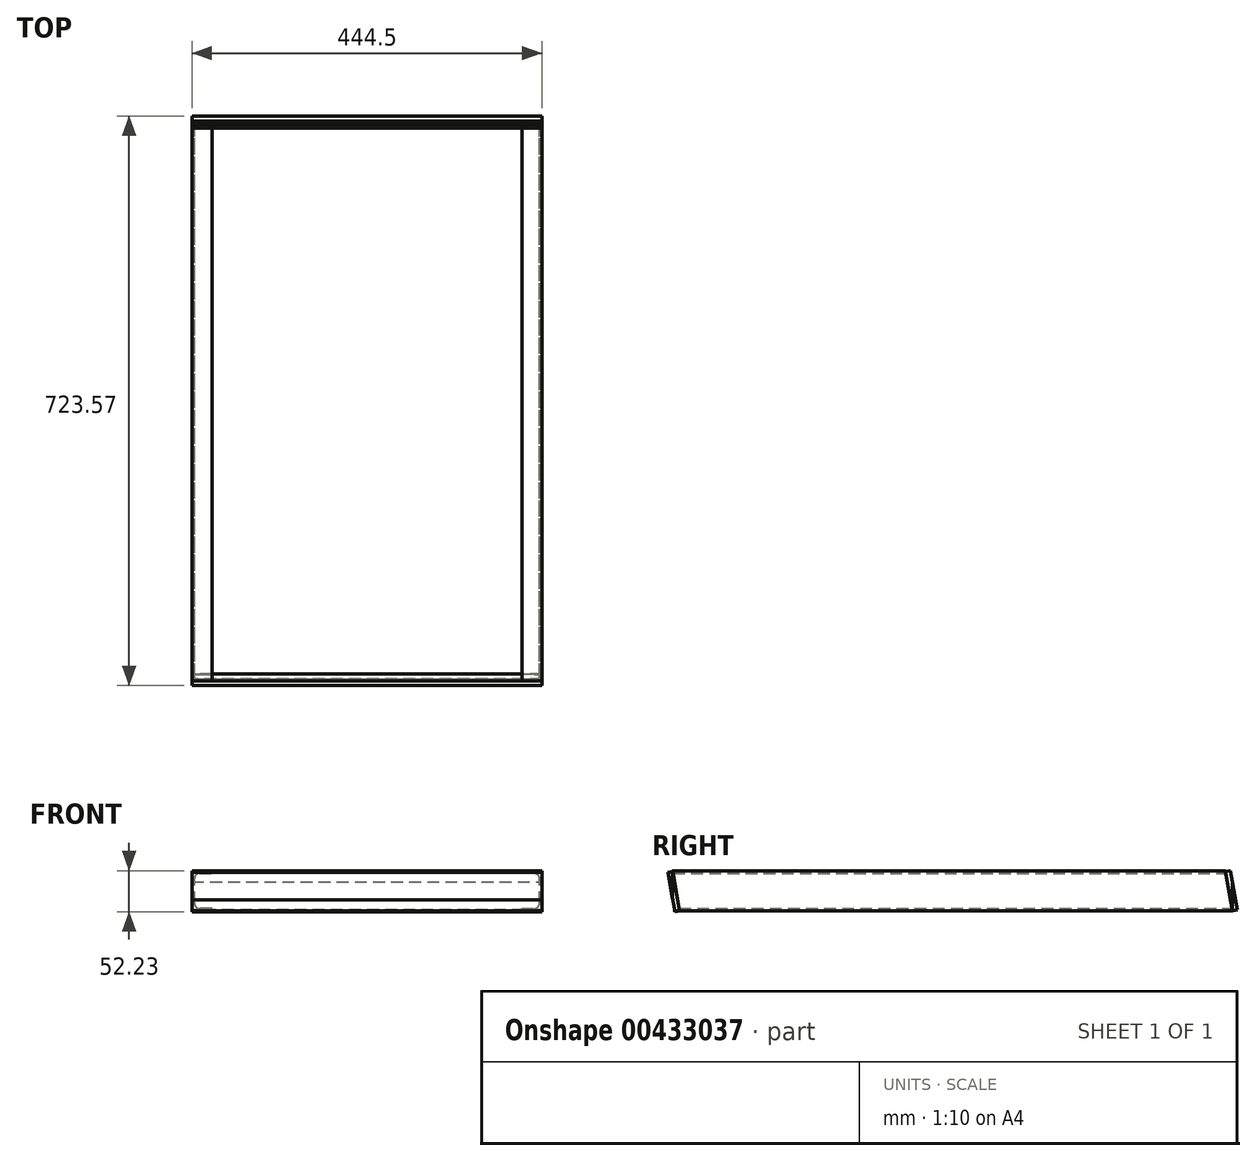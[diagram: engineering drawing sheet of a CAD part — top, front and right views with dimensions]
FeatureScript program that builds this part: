
annotation { "Feature Type Name" : "Feature", "Feature Type Description" : "" }
export const myFeature = defineFeature(function(context is Context, id is Id, definition is map)
    precondition{}
    {
        {
            var Q0;
            Q0=qCreatedBy(makeId("Front.planeOp"),FACE);
            var sketch = newSketch(context, id + "F0", { "sketchPlane" : qUnion([Q0])});
            skLineSegment(sketch, "E0", {"start": v(0, 0) * mm, "end": v(0, 50.8) * mm});
            skLineSegment(sketch, "E1", {"start": v(0, 50.8) * mm, "end": v(25.4, 50.8) * mm});
            skLineSegment(sketch, "E2", {"start": v(25.4, 50.8) * mm, "end": v(25.4, 47.63) * mm});
            skLineSegment(sketch, "E3", {"start": v(25.4, 47.63) * mm, "end": v(9.52, 47.63) * mm});
            skLineSegment(sketch, "E4", {"start": v(3.17, 41.28) * mm, "end": v(3.18, 9.52) * mm});
            skLineSegment(sketch, "E5", {"start": v(9.53, 3.17) * mm, "end": v(25.4, 3.18) * mm});
            skLineSegment(sketch, "E6", {"start": v(25.4, 3.18) * mm, "end": v(25.4, 0) * mm});
            skLineSegment(sketch, "E7", {"start": v(25.4, 0) * mm, "end": v(0, 0) * mm});
            skLineSegment(sketch, "E8", {"start": v(419.1, 0) * mm, "end": v(444.5, 0) * mm});
            skLineSegment(sketch, "E9", {"start": v(444.5, 0) * mm, "end": v(444.5, 50.8) * mm});
            skLineSegment(sketch, "E10", {"start": v(444.5, 50.8) * mm, "end": v(419.1, 50.8) * mm});
            skLineSegment(sketch, "E11", {"start": v(419.1, 50.8) * mm, "end": v(419.1, 47.63) * mm});
            skLineSegment(sketch, "E12", {"start": v(419.1, 47.63) * mm, "end": v(434.98, 47.63) * mm});
            skLineSegment(sketch, "E13", {"start": v(441.33, 41.28) * mm, "end": v(441.33, 9.53) * mm});
            skLineSegment(sketch, "E14", {"start": v(434.98, 3.18) * mm, "end": v(419.1, 3.18) * mm});
            skLineSegment(sketch, "E15", {"start": v(419.1, 3.18) * mm, "end": v(419.1, 0) * mm});
            skPoint(sketch, "E16.visualSharp", {"position": v(3.17, 47.62) * mm});
            skArc(sketch, "E16.filletArc", {"start": v(9.52, 47.63) * mm, "mid": v(5.03, 45.77) * mm, "end": v(3.17, 41.28) * mm});
            skPoint(sketch, "E17.visualSharp", {"position": v(3.18, 3.17) * mm});
            skArc(sketch, "E17.filletArc", {"start": v(3.18, 9.52) * mm, "mid": v(5.03, 5.03) * mm, "end": v(9.53, 3.17) * mm});
            skPoint(sketch, "E18.visualSharp", {"position": v(441.33, 47.63) * mm});
            skArc(sketch, "E18.filletArc", {"start": v(441.33, 41.28) * mm, "mid": v(439.47, 45.77) * mm, "end": v(434.98, 47.63) * mm});
            skPoint(sketch, "E19.visualSharp", {"position": v(441.33, 3.18) * mm});
            skArc(sketch, "E19.filletArc", {"start": v(434.98, 3.18) * mm, "mid": v(439.47, 5.03) * mm, "end": v(441.33, 9.53) * mm});
            skSolve(sketch);
        }
        {
            var Q0;
            Q0=makeQuery(id+"F0.imprint","IMPRINT",FACE,{"disambiguationData":[TD([[makeQuery(id+"F0.imprint","IMPRINT",EDGE,{"derivedFrom":sQuery(id+"F0.wireOp",EDGE,"E0")}),-1.0]])]});
            var Q1;
            Q1=makeQuery(id+"F0.imprint","IMPRINT",FACE,{"disambiguationData":[TD([[makeQuery(id+"F0.imprint","IMPRINT",EDGE,{"derivedFrom":sQuery(id+"F0.wireOp",EDGE,"E8")}),1.0]])]});
            extrude(context, id + "F1", {"entities" : qUnion([Q0, Q1]), "depth" : 711.2 * mm, "offsetDistance" : 25.4 * mm});
        }
        {
            var Q0;
            Q0=qCreatedBy(makeId("Right.planeOp"),FACE);
            var sketch = newSketch(context, id + "F2", { "sketchPlane" : qUnion([Q0])});
            skLineSegment(sketch, "E20", {"start": v(0, 0) * mm, "end": v(0, 50.8) * mm});
            skLineSegment(sketch, "E21", {"start": v(0, 50.8) * mm, "end": v(-8.96, 50.8) * mm});
            skLineSegment(sketch, "E22", {"start": v(-8.96, 50.8) * mm, "end": v(0, 0) * mm});
            skLineSegment(sketch, "E23", {"start": v(-702.24, 0) * mm, "end": v(-711.2, 50.8) * mm});
            skLineSegment(sketch, "E24", {"start": v(-711.2, 50.8) * mm, "end": v(-711.2, 0) * mm});
            skLineSegment(sketch, "E25", {"start": v(-711.2, 0) * mm, "end": v(-702.24, 0) * mm});
            skSolve(sketch);
        }
        {
            var Q0;
            Q0=makeQuery(id+"F2.imprint","IMPRINT",FACE,{"disambiguationData":[TD([[makeQuery(id+"F2.imprint","IMPRINT",EDGE,{"derivedFrom":sQuery(id+"F2.wireOp",EDGE,"E20")}),1.0]])]});
            var Q1;
            Q1=makeQuery(id+"F2.imprint","IMPRINT",FACE,{"disambiguationData":[TD([[makeQuery(id+"F2.imprint","IMPRINT",EDGE,{"derivedFrom":sQuery(id+"F2.wireOp",EDGE,"E23")}),1.0]])]});
            var Q2;
            Q2=makeQuery(id+"F1.opExtrude","SWEPT_FACE",FACE,{"disambiguationData":[OSD([sQuery(id+"F0.wireOp",EDGE,"E9")])]});
            extrude(context, id + "F3", {"entities" : qUnion([Q0, Q1]), "operationType" : NewBodyOperationType.REMOVE, "endBound" : BoundingType.THROUGH_ALL, "endBoundEntityFace" : qUnion([Q2]), "depth" : 25.4 * mm, "offsetDistance" : 25.4 * mm});
        }
        {
            var Q0;
            Q0=qCreatedBy(makeId("Right.planeOp"),FACE);
            var sketch = newSketch(context, id + "F4", { "sketchPlane" : qUnion([Q0])});
            skLineSegment(sketch, "E26", {"start": v(0, 0) * mm, "end": v(-8.82, 50.03) * mm});
            skLineSegment(sketch, "E27", {"start": v(-8.82, 50.03) * mm, "end": v(-2.57, 51.13) * mm});
            skLineSegment(sketch, "E28", {"start": v(-2.57, 51.13) * mm, "end": v(6.25, 1.1) * mm});
            skLineSegment(sketch, "E29", {"start": v(6.25, 1.1) * mm, "end": v(0, 0) * mm});
            skLineSegment(sketch, "E30", {"start": v(-702.24, 0) * mm, "end": v(-711.06, 50.03) * mm});
            skLineSegment(sketch, "E31", {"start": v(-711.06, 50.03) * mm, "end": v(-717.32, 48.93) * mm});
            skLineSegment(sketch, "E32", {"start": v(-717.32, 48.93) * mm, "end": v(-708.5, -1.1) * mm});
            skLineSegment(sketch, "E33", {"start": v(-708.5, -1.1) * mm, "end": v(-702.24, 0) * mm});
            skSolve(sketch);
        }
        {
            var Q0;
            Q0=makeQuery(id+"F4.imprint","IMPRINT",FACE,{"disambiguationData":[TD([[makeQuery(id+"F4.imprint","IMPRINT",EDGE,{"derivedFrom":sQuery(id+"F4.wireOp",EDGE,"E30")}),1.0]])]});
            var Q1;
            Q1=makeQuery(id+"F4.imprint","IMPRINT",FACE,{"disambiguationData":[TD([[makeQuery(id+"F4.imprint","IMPRINT",EDGE,{"derivedFrom":sQuery(id+"F4.wireOp",EDGE,"E26")}),-1.0]])]});
            extrude(context, id + "F5", {"entities" : qUnion([Q0, Q1]), "depth" : 444.5 * mm, "offsetDistance" : 25.4 * mm});
        }
    });
